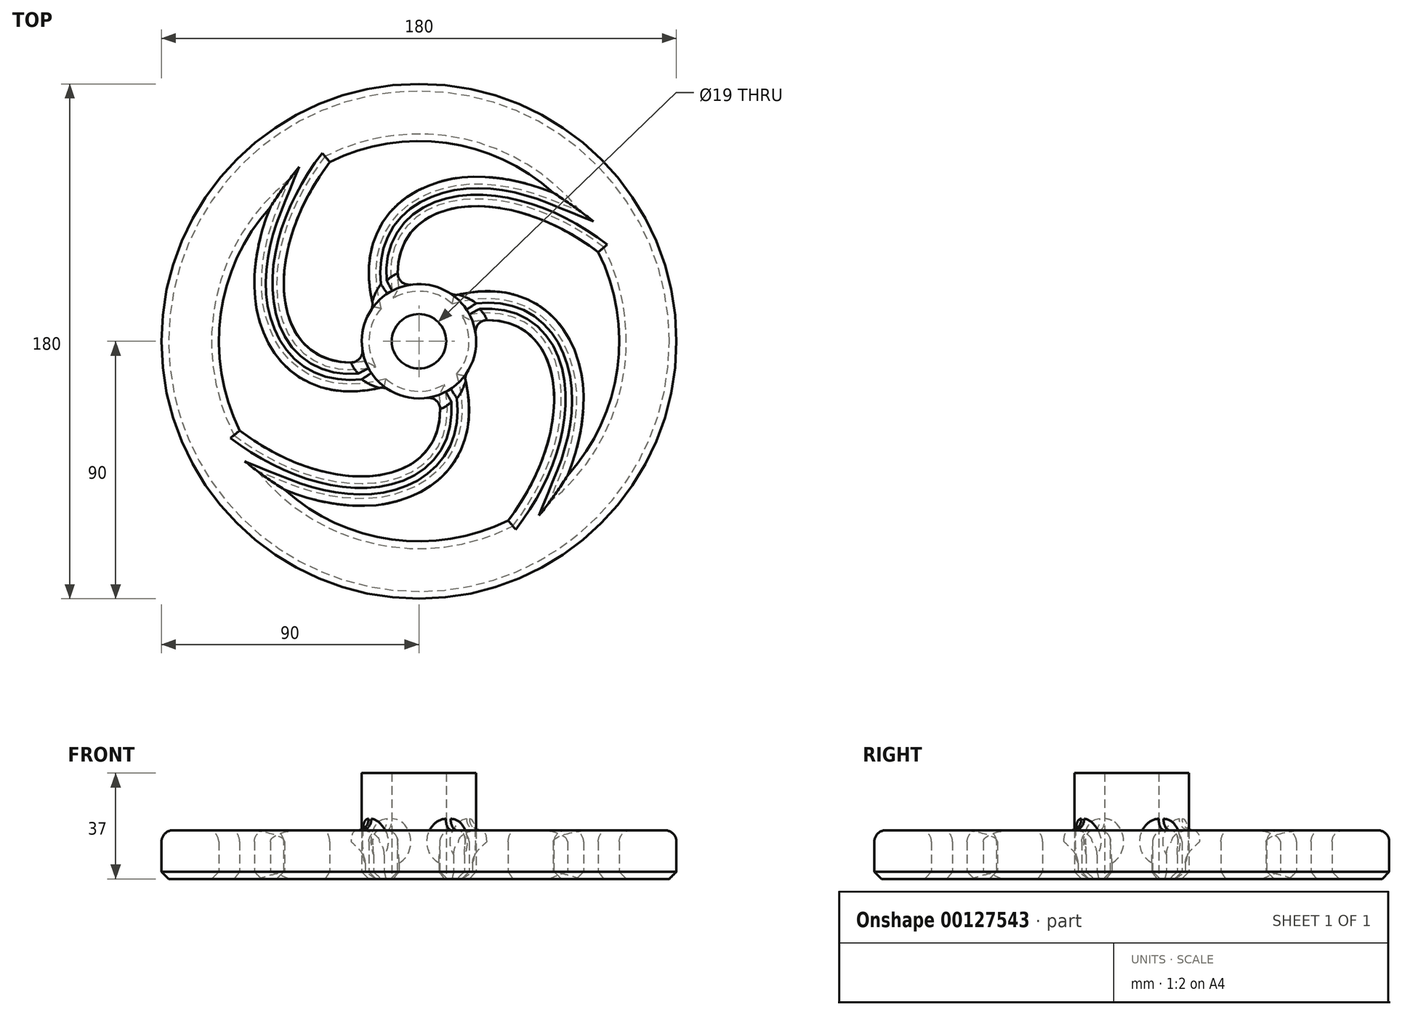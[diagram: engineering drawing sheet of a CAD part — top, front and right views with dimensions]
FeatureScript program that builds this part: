
annotation { "Feature Type Name" : "Feature", "Feature Type Description" : "" }
export const myFeature = defineFeature(function(context is Context, id is Id, definition is map)
    precondition{}
    {
        {
            var Q0;
            Q0=qCreatedBy(makeId("Top.planeOp"),FACE);
            var sketch = newSketch(context, id + "F0", { "sketchPlane" : qUnion([Q0])});
            skCircle(sketch, "E0", {"center": v(0, 0) * mm, "radius": 90 * mm});
            skCircle(sketch, "E1", {"center": v(0, 0) * mm, "radius": 70 * mm});
            skCircle(sketch, "E2", {"center": v(0, 0) * mm, "radius": 9.5 * mm});
            skCircle(sketch, "E3", {"center": v(0, 0) * mm, "radius": 20 * mm});
            skFitSpline(sketch, "E4", {"points": [v(0, 0) * mm, v(0, 90) * mm], "startDerivative": vector(-175.85, -97.64) * mm, "endDerivative": vector(201.76, 118.77) * mm});
            skFitSpline(sketch, "E5.0", {"points": [v(4.85, -8.74) * mm, v(0.77, -11) * mm, v(-5.16, -13.73) * mm, v(-12.74, -16.05) * mm, v(-18.28, -17.12) * mm, v(-23.67, -17.52) * mm, v(-28.89, -17.2) * mm, v(-33.88, -16.16) * mm, v(-38.56, -14.38) * mm, v(-42.83, -11.89) * mm, v(-46.58, -8.78) * mm, v(-49.76, -5.16) * mm, v(-52.35, -1.14) * mm, v(-54.36, 3.19) * mm, v(-56.32, 9.27) * mm, v(-57.5, 17.36) * mm, v(-57.08, 27.6) * mm, v(-54.92, 38.21) * mm, v(-51.06, 49.03) * mm, v(-45.47, 59.85) * mm, v(-38.14, 70.47) * mm, v(-26, 84.06) * mm, v(-14.18, 93.26) * mm, v(-5.07, 98.62) * mm]});
            skSolve(sketch);
        }
        {
            var Q0;
            Q0=makeQuery(id+"F0.imprint","IMPRINT",FACE,{"disambiguationData":[TD([[makeQuery(id+"F0.imprint","IMPRINT",EDGE,{"derivedFrom":sQuery(id+"F0.wireOp",EDGE,"E0")}),1.0]])]});
            var Q1;
            {var subQ0=sQuery(id+"F0.wireOp",EDGE,"E4");Q1=makeQuery(id+"F0.imprint","IMPRINT",FACE,{"disambiguationData":[TD([[makeQuery(id+"F0.imprint","IMPRINT",EDGE,{"derivedFrom":subQ0}),1.0]])]});}
            var Q2;
            Q2=makeQuery(id+"F0.imprint","IMPRINT",FACE,{"disambiguationData":[TD([[makeQuery(id+"F0.imprint","IMPRINT",EDGE,{"derivedFrom":sQuery(id+"F0.wireOp",EDGE,"E2")}),-1.0]])]});
            extrude(context, id + "F1", {"entities" : qUnion([Q0, Q1, Q2]), "depth" : 17 * mm});
        }
        {
            var Q0;
            Q0=qCreatedBy(makeId("Front.planeOp"),FACE);
            var sketch = newSketch(context, id + "F2", { "sketchPlane" : qUnion([Q0])});
            skLineSegment(sketch, "E6", {"start": v(0, 7.44) * mm, "end": v(0, 182.95) * mm});
            skSolve(sketch);
        }
        {
            var Q0;
            Q0=makeQuery(id+"F1.opExtrude","SWEPT_BODY",BODY,{"disambiguationData":[OSD([sQuery(id+"F0.wireOp",EDGE,"E0"),sQuery(id+"F0.wireOp",EDGE,"E1"),sQuery(id+"F0.wireOp",EDGE,"E2"),sQuery(id+"F0.wireOp",EDGE,"E3"),sQuery(id+"F0.wireOp",EDGE,"E4"),sQuery(id+"F0.wireOp",EDGE,"E5.0")])]});
            var Q1;
            Q1=sQuery(id+"F2.wireOp",EDGE,"E6");
            transform(context, id + "F3", {"entities" : qUnion([Q0]), "transformType" : TransformType.ROTATION, "transformAxis" : qUnion([Q1]), "angle" : 90 * degree, "makeCopy" : true});
        }
        {
            var Q0;
            Q0=makeQuery(id+"F1.opExtrude","SWEPT_BODY",BODY,{"disambiguationData":[OSD([sQuery(id+"F0.wireOp",EDGE,"E0"),sQuery(id+"F0.wireOp",EDGE,"E1"),sQuery(id+"F0.wireOp",EDGE,"E2"),sQuery(id+"F0.wireOp",EDGE,"E3"),sQuery(id+"F0.wireOp",EDGE,"E4"),sQuery(id+"F0.wireOp",EDGE,"E5.0")])]});
            var Q1;
            Q1=sQuery(id+"F2.wireOp",EDGE,"E6");
            transform(context, id + "F4", {"entities" : qUnion([Q0]), "transformType" : TransformType.ROTATION, "transformAxis" : qUnion([Q1]), "angle" : 180 * degree, "makeCopy" : true});
        }
        {
            var Q0;
            Q0=makeQuery(id+"F1.opExtrude","SWEPT_BODY",BODY,{"disambiguationData":[OSD([sQuery(id+"F0.wireOp",EDGE,"E0"),sQuery(id+"F0.wireOp",EDGE,"E1"),sQuery(id+"F0.wireOp",EDGE,"E2"),sQuery(id+"F0.wireOp",EDGE,"E3"),sQuery(id+"F0.wireOp",EDGE,"E4"),sQuery(id+"F0.wireOp",EDGE,"E5.0")])]});
            var Q1;
            Q1=sQuery(id+"F2.wireOp",EDGE,"E6");
            transform(context, id + "F5", {"entities" : qUnion([Q0]), "transformType" : TransformType.ROTATION, "transformAxis" : qUnion([Q1]), "angle" : 270 * degree, "makeCopy" : true});
        }
        {
            var Q0;
            Q0=makeQuery(id+"F0.imprint","IMPRINT",FACE,{"disambiguationData":[TD([[makeQuery(id+"F0.imprint","IMPRINT",EDGE,{"derivedFrom":sQuery(id+"F0.wireOp",EDGE,"E2")}),-1.0]])]});
            extrude(context, id + "F6", {"entities" : qUnion([Q0]), "operationType" : NewBodyOperationType.ADD, "depth" : 37 * mm});
        }
        {
            var Q0;
            Q0=makeQuery(id+"F1.opExtrude","CAP_EDGE",EDGE,{"disambiguationData":[OSD([sQuery(id+"F0.wireOp",EDGE,"E0")])],"isStart":true});
            var Q1;
            {var subQ0=sQuery(id+"F0.wireOp",EDGE,"E5.0");var subQ1=sQuery(id+"F0.wireOp",EDGE,"E1");Q1=makeQuery(id+"F6.boolean.opBoolean","SPLIT",EDGE,{"disambiguationData":[TD([makeQuery(id+"F1.opExtrude","SWEPT_FACE",FACE,{"disambiguationData":[OSD([subQ0])]})])],"derivedFrom":makeQuery(id+"F1.opExtrude","CAP_EDGE",EDGE,{"disambiguationData":[OSD([subQ1])],"isStart":true})});}
            var Q2;
            {var subQ0=sQuery(id+"F0.wireOp",EDGE,"E5.0");var subQ1=sQuery(id+"F0.wireOp",EDGE,"E1");Q2=makeQuery(id+"F6.boolean.opBoolean","SPLIT",EDGE,{"disambiguationData":[TD([makeQuery(id+"F3.opPattern","COPY",FACE,{"derivedFrom":makeQuery(id+"F1.opExtrude","SWEPT_FACE",FACE,{"disambiguationData":[OSD([subQ0])]}),"instanceName":"1"})])],"derivedFrom":makeQuery(id+"F1.opExtrude","CAP_EDGE",EDGE,{"disambiguationData":[OSD([subQ1])],"isStart":true})});}
            var Q3;
            {var subQ0=sQuery(id+"F0.wireOp",EDGE,"E1");var subQ1=sQuery(id+"F0.wireOp",EDGE,"E5.0");Q3=makeQuery(id+"F6.boolean.opBoolean","SPLIT",EDGE,{"disambiguationData":[TD([makeQuery(id+"F4.opPattern","COPY",FACE,{"derivedFrom":makeQuery(id+"F1.opExtrude","SWEPT_FACE",FACE,{"disambiguationData":[OSD([subQ1])]}),"instanceName":"1"})])],"derivedFrom":makeQuery(id+"F1.opExtrude","CAP_EDGE",EDGE,{"disambiguationData":[OSD([subQ0])],"isStart":true})});}
            var Q4;
            {var subQ0=sQuery(id+"F0.wireOp",EDGE,"E4");var subQ2=sQuery(id+"F0.wireOp",EDGE,"E1");Q4=makeQuery(id+"F6.boolean.opBoolean","SPLIT",EDGE,{"disambiguationData":[TD([makeQuery(id+"F1.opExtrude","SWEPT_FACE",FACE,{"disambiguationData":[OSD([subQ0])]})])],"derivedFrom":makeQuery(id+"F1.opExtrude","CAP_EDGE",EDGE,{"disambiguationData":[OSD([subQ2])],"isStart":true})});}
            var Q5;
            Q5=makeQuery(id+"F1.opExtrude","CAP_EDGE",EDGE,{"disambiguationData":[OSD([sQuery(id+"F0.wireOp",EDGE,"E4")])],"isStart":true});
            var Q6;
            Q6=makeQuery(id+"F1.opExtrude","CAP_EDGE",EDGE,{"disambiguationData":[OSD([sQuery(id+"F0.wireOp",EDGE,"E5.0")])],"isStart":true});
            var Q7;
            {var subQ0=sQuery(id+"F0.wireOp",EDGE,"E5.0");var subQ2=sQuery(id+"F0.wireOp",EDGE,"E3");Q7=makeQuery(id+"F6.boolean.opBoolean","SPLIT",EDGE,{"disambiguationData":[TD([makeQuery(id+"F1.opExtrude","SWEPT_FACE",FACE,{"disambiguationData":[OSD([subQ0])]})])],"derivedFrom":makeQuery(id+"F1.opExtrude","CAP_EDGE",EDGE,{"disambiguationData":[OSD([subQ2])],"isStart":true})});}
            var Q8;
            Q8=makeQuery(id+"F3.opPattern","COPY",EDGE,{"derivedFrom":makeQuery(id+"F1.opExtrude","CAP_EDGE",EDGE,{"disambiguationData":[OSD([sQuery(id+"F0.wireOp",EDGE,"E4")])],"isStart":true}),"instanceName":"1"});
            var Q9;
            Q9=makeQuery(id+"F3.opPattern","COPY",EDGE,{"derivedFrom":makeQuery(id+"F1.opExtrude","CAP_EDGE",EDGE,{"disambiguationData":[OSD([sQuery(id+"F0.wireOp",EDGE,"E5.0")])],"isStart":true}),"instanceName":"1"});
            var Q10;
            Q10=makeQuery(id+"F4.opPattern","COPY",EDGE,{"derivedFrom":makeQuery(id+"F1.opExtrude","CAP_EDGE",EDGE,{"disambiguationData":[OSD([sQuery(id+"F0.wireOp",EDGE,"E4")])],"isStart":true}),"instanceName":"1"});
            var Q11;
            {var subQ0=sQuery(id+"F0.wireOp",EDGE,"E5.0");var subQ2=sQuery(id+"F0.wireOp",EDGE,"E3");Q11=makeQuery(id+"F6.boolean.opBoolean","SPLIT",EDGE,{"disambiguationData":[TD([makeQuery(id+"F3.opPattern","COPY",FACE,{"derivedFrom":makeQuery(id+"F1.opExtrude","SWEPT_FACE",FACE,{"disambiguationData":[OSD([subQ0])]}),"instanceName":"1"})])],"derivedFrom":makeQuery(id+"F1.opExtrude","CAP_EDGE",EDGE,{"disambiguationData":[OSD([subQ2])],"isStart":true})});}
            var Q12;
            Q12=makeQuery(id+"F4.opPattern","COPY",EDGE,{"derivedFrom":makeQuery(id+"F1.opExtrude","CAP_EDGE",EDGE,{"disambiguationData":[OSD([sQuery(id+"F0.wireOp",EDGE,"E5.0")])],"isStart":true}),"instanceName":"1"});
            var Q13;
            {var subQ1=sQuery(id+"F0.wireOp",EDGE,"E5.0");var subQ2=sQuery(id+"F0.wireOp",EDGE,"E3");Q13=makeQuery(id+"F6.boolean.opBoolean","SPLIT",EDGE,{"disambiguationData":[TD([makeQuery(id+"F4.opPattern","COPY",FACE,{"derivedFrom":makeQuery(id+"F1.opExtrude","SWEPT_FACE",FACE,{"disambiguationData":[OSD([subQ1])]}),"instanceName":"1"})])],"derivedFrom":makeQuery(id+"F1.opExtrude","CAP_EDGE",EDGE,{"disambiguationData":[OSD([subQ2])],"isStart":true})});}
            var Q14;
            Q14=makeQuery(id+"F5.opPattern","COPY",EDGE,{"derivedFrom":makeQuery(id+"F1.opExtrude","CAP_EDGE",EDGE,{"disambiguationData":[OSD([sQuery(id+"F0.wireOp",EDGE,"E4")])],"isStart":true}),"instanceName":"1"});
            var Q15;
            Q15=makeQuery(id+"F5.opPattern","COPY",EDGE,{"derivedFrom":makeQuery(id+"F1.opExtrude","CAP_EDGE",EDGE,{"disambiguationData":[OSD([sQuery(id+"F0.wireOp",EDGE,"E5.0")])],"isStart":true}),"instanceName":"1"});
            var Q16;
            {var subQ1=sQuery(id+"F0.wireOp",EDGE,"E4");var subQ2=sQuery(id+"F0.wireOp",EDGE,"E3");Q16=makeQuery(id+"F6.boolean.opBoolean","SPLIT",EDGE,{"disambiguationData":[TD([makeQuery(id+"F1.opExtrude","SWEPT_FACE",FACE,{"disambiguationData":[OSD([subQ1])]})])],"derivedFrom":makeQuery(id+"F1.opExtrude","CAP_EDGE",EDGE,{"disambiguationData":[OSD([subQ2])],"isStart":true})});}
            chamfer(context, id + "F7", {"entities" : qUnion([Q0, Q1, Q2, Q3, Q4, Q5, Q6, Q7, Q8, Q9, Q10, Q11, Q12, Q13, Q14, Q15, Q16]), "width" : 2.5 * mm});
        }
        {
            var Q0;
            {var subQ0=makeQuery(id+"F1.opExtrude","CAP_FACE",FACE,{"disambiguationData":[OSD([sQuery(id+"F0.wireOp",EDGE,"E0"),sQuery(id+"F0.wireOp",EDGE,"E1"),sQuery(id+"F0.wireOp",EDGE,"E2"),sQuery(id+"F0.wireOp",EDGE,"E3"),sQuery(id+"F0.wireOp",EDGE,"E4"),sQuery(id+"F0.wireOp",EDGE,"E5.0")])],"isStart":false});Q0=makeQuery(id+"F6.boolean.opBoolean","MERGE",FACE,{"derivedFrom":[subQ0,makeQuery(id+"F3.opPattern","COPY",FACE,{"derivedFrom":subQ0,"instanceName":"1"}),makeQuery(id+"F4.opPattern","COPY",FACE,{"derivedFrom":subQ0,"instanceName":"1"}),makeQuery(id+"F5.opPattern","COPY",FACE,{"derivedFrom":subQ0,"instanceName":"1"})]});}
            fillet(context, id + "F8", {"entities" : qUnion([Q0]), "radius" : 4 * mm, "tangentPropagation" : true, "allowEdgeOverflow" : false});
        }
    });
